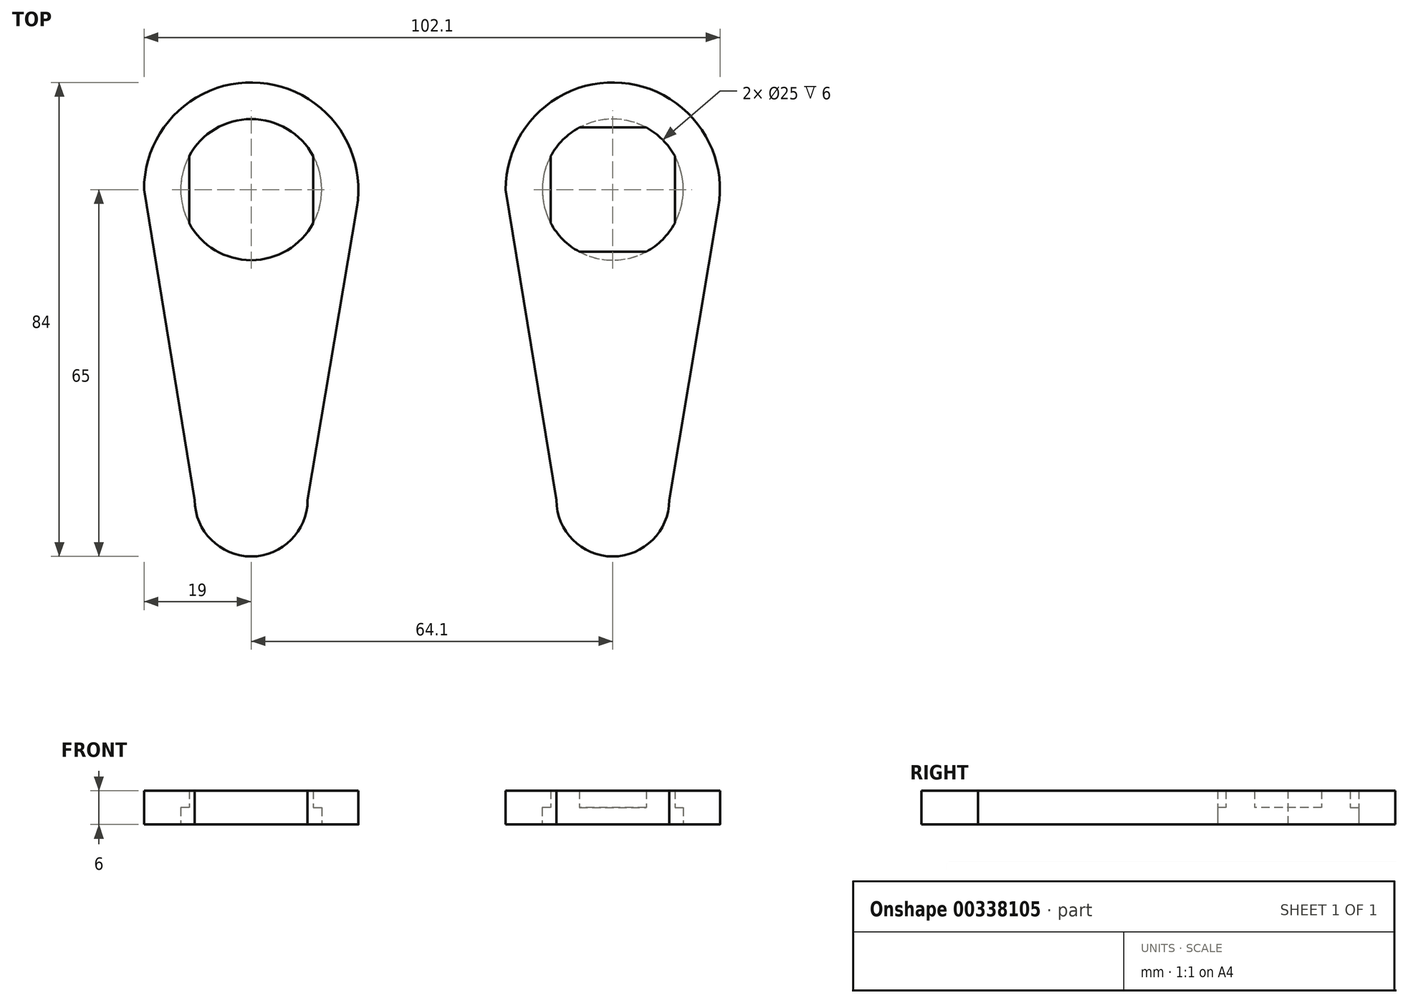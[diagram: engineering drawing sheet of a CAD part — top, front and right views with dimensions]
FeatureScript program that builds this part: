
annotation { "Feature Type Name" : "Feature", "Feature Type Description" : "" }
export const myFeature = defineFeature(function(context is Context, id is Id, definition is map)
    precondition{}
    {
        {
            var Q0;
            Q0=qCreatedBy(makeId("Top.planeOp"),FACE);
            var sketch = newSketch(context, id + "F0", { "sketchPlane" : qUnion([Q0])});
            skLineSegment(sketch, "E0.bottom", {"start": v(-11, 11) * mm, "end": v(11, 11) * mm});
            skLineSegment(sketch, "E0.top", {"start": v(-11, -11) * mm, "end": v(11, -11) * mm});
            skLineSegment(sketch, "E0.left", {"start": v(-11, 11) * mm, "end": v(-11, -11) * mm});
            skLineSegment(sketch, "E0.right", {"start": v(11, 11) * mm, "end": v(11, -11) * mm});
            skCircle(sketch, "E1", {"center": v(0, 0) * mm, "radius": 12.5 * mm});
            skCircle(sketch, "E2", {"center": v(0, 0) * mm, "radius": 19 * mm});
            skCircle(sketch, "E3", {"center": v(0, -55) * mm, "radius": 10 * mm});
            skLineSegment(sketch, "E4", {"start": v(-19, 0) * mm, "end": v(-10, -55) * mm});
            skLineSegment(sketch, "E5", {"start": v(10, -55) * mm, "end": v(19.27, 0) * mm});
            skSolve(sketch);
        }
        {
            var Q0;
            Q0 = qSketchRegion(id + "F0", true);
            var Q1;
            {var subQ0=sQuery(id+"F0.wireOp",EDGE,"E0.left");var subQ1=sQuery(id+"F0.wireOp",EDGE,"E0.bottom");var subQ2=makeQuery(id+"F0.imprint","INTERSECT",VERTEX,{"derivedFrom":[subQ1,subQ0]});Q1=makeQuery(id+"F0.imprint","IMPRINT",FACE,{"disambiguationData":[TD([[makeQuery(id+"F0.imprint","IMPRINT",EDGE,{"disambiguationData":[TD([[subQ2,-1.0]])],"derivedFrom":subQ1}),-1.0]])]});}
            var Q2;
            {var subQ0=sQuery(id+"F0.wireOp",EDGE,"E1");var subQ1=sQuery(id+"F0.wireOp",EDGE,"E0.bottom");var subQ2=makeQuery(id+"F0.imprint","INTERSECT",VERTEX,{"disambiguationData":[OD(0.0)],"derivedFrom":[subQ1,subQ0]});Q2=makeQuery(id+"F0.imprint","IMPRINT",FACE,{"disambiguationData":[TD([[makeQuery(id+"F0.imprint","IMPRINT",EDGE,{"disambiguationData":[TD([[subQ2,-1.0]])],"derivedFrom":subQ1}),1.0]])]});}
            var Q3;
            {var subQ0=sQuery(id+"F0.wireOp",EDGE,"E0.right");var subQ1=sQuery(id+"F0.wireOp",EDGE,"E0.bottom");var subQ2=makeQuery(id+"F0.imprint","INTERSECT",VERTEX,{"derivedFrom":[subQ1,subQ0]});Q3=makeQuery(id+"F0.imprint","IMPRINT",FACE,{"disambiguationData":[TD([[makeQuery(id+"F0.imprint","IMPRINT",EDGE,{"disambiguationData":[TD([[subQ2,1.0]])],"derivedFrom":subQ1}),-1.0]])]});}
            var Q4;
            {var subQ0=sQuery(id+"F0.wireOp",EDGE,"E0.right");var subQ1=sQuery(id+"F0.wireOp",EDGE,"E0.top");var subQ2=makeQuery(id+"F0.imprint","INTERSECT",VERTEX,{"derivedFrom":[subQ1,subQ0]});Q4=makeQuery(id+"F0.imprint","IMPRINT",FACE,{"disambiguationData":[TD([[makeQuery(id+"F0.imprint","IMPRINT",EDGE,{"disambiguationData":[TD([[subQ2,1.0]])],"derivedFrom":subQ1}),1.0]])]});}
            var Q5;
            {var subQ0=sQuery(id+"F0.wireOp",EDGE,"E1");var subQ1=sQuery(id+"F0.wireOp",EDGE,"E0.right");var subQ2=makeQuery(id+"F0.imprint","INTERSECT",VERTEX,{"disambiguationData":[OD(0.0)],"derivedFrom":[subQ1,subQ0]});Q5=makeQuery(id+"F0.imprint","IMPRINT",FACE,{"disambiguationData":[TD([[makeQuery(id+"F0.imprint","IMPRINT",EDGE,{"disambiguationData":[TD([[subQ2,-1.0]])],"derivedFrom":subQ1}),1.0]])]});}
            var Q6;
            {var subQ0=sQuery(id+"F0.wireOp",EDGE,"E0.left");var subQ1=sQuery(id+"F0.wireOp",EDGE,"E0.top");var subQ2=makeQuery(id+"F0.imprint","INTERSECT",VERTEX,{"derivedFrom":[subQ1,subQ0]});Q6=makeQuery(id+"F0.imprint","IMPRINT",FACE,{"disambiguationData":[TD([[makeQuery(id+"F0.imprint","IMPRINT",EDGE,{"disambiguationData":[TD([[subQ2,-1.0]])],"derivedFrom":subQ1}),1.0]])]});}
            var Q7;
            {var subQ0=sQuery(id+"F0.wireOp",EDGE,"E1");var subQ1=sQuery(id+"F0.wireOp",EDGE,"E0.top");var subQ2=makeQuery(id+"F0.imprint","INTERSECT",VERTEX,{"disambiguationData":[OD(0.0)],"derivedFrom":[subQ1,subQ0]});Q7=makeQuery(id+"F0.imprint","IMPRINT",FACE,{"disambiguationData":[TD([[makeQuery(id+"F0.imprint","IMPRINT",EDGE,{"disambiguationData":[TD([[subQ2,-1.0]])],"derivedFrom":subQ1}),-1.0]])]});}
            var Q8;
            {var subQ0=sQuery(id+"F0.wireOp",EDGE,"E1");var subQ1=sQuery(id+"F0.wireOp",EDGE,"E0.left");var subQ2=makeQuery(id+"F0.imprint","INTERSECT",VERTEX,{"disambiguationData":[OD(0.0)],"derivedFrom":[subQ1,subQ0]});Q8=makeQuery(id+"F0.imprint","IMPRINT",FACE,{"disambiguationData":[TD([[makeQuery(id+"F0.imprint","IMPRINT",EDGE,{"disambiguationData":[TD([[subQ2,-1.0]])],"derivedFrom":subQ1}),-1.0]])]});}
            extrude(context, id + "F1", {"entities" : qUnion([Q0, Q1, Q2, Q3, Q4, Q5, Q6, Q7, Q8]), "depth" : 3 * mm});
        }
        {
            var Q0;
            {var subQ1=sQuery(id+"F0.wireOp",EDGE,"E0.left");var subQ5=sQuery(id+"F0.wireOp",EDGE,"E0.bottom");var subQ10=makeQuery(id+"F0.imprint","INTERSECT",VERTEX,{"derivedFrom":[subQ5,subQ1]});Q0=makeQuery(id+"F0.imprint","IMPRINT",FACE,{"disambiguationData":[TD([[makeQuery(id+"F0.imprint","IMPRINT",EDGE,{"disambiguationData":[TD([[subQ10,-1.0]])],"derivedFrom":subQ5}),1.0]])]});}
            var Q1;
            {var subQ0=sQuery(id+"F0.wireOp",EDGE,"E0.left");var subQ1=sQuery(id+"F0.wireOp",EDGE,"E0.bottom");var subQ2=makeQuery(id+"F0.imprint","INTERSECT",VERTEX,{"derivedFrom":[subQ1,subQ0]});Q1=makeQuery(id+"F0.imprint","IMPRINT",FACE,{"disambiguationData":[TD([[makeQuery(id+"F0.imprint","IMPRINT",EDGE,{"disambiguationData":[TD([[subQ2,-1.0]])],"derivedFrom":subQ1}),-1.0]])]});}
            var Q2;
            {var subQ0=sQuery(id+"F0.wireOp",EDGE,"E0.right");var subQ1=sQuery(id+"F0.wireOp",EDGE,"E0.bottom");var subQ2=makeQuery(id+"F0.imprint","INTERSECT",VERTEX,{"derivedFrom":[subQ1,subQ0]});Q2=makeQuery(id+"F0.imprint","IMPRINT",FACE,{"disambiguationData":[TD([[makeQuery(id+"F0.imprint","IMPRINT",EDGE,{"disambiguationData":[TD([[subQ2,1.0]])],"derivedFrom":subQ1}),-1.0]])]});}
            var Q3;
            {var subQ0=sQuery(id+"F0.wireOp",EDGE,"E0.right");var subQ1=sQuery(id+"F0.wireOp",EDGE,"E0.top");var subQ2=makeQuery(id+"F0.imprint","INTERSECT",VERTEX,{"derivedFrom":[subQ1,subQ0]});Q3=makeQuery(id+"F0.imprint","IMPRINT",FACE,{"disambiguationData":[TD([[makeQuery(id+"F0.imprint","IMPRINT",EDGE,{"disambiguationData":[TD([[subQ2,1.0]])],"derivedFrom":subQ1}),1.0]])]});}
            var Q4;
            {var subQ0=sQuery(id+"F0.wireOp",EDGE,"E0.left");var subQ1=sQuery(id+"F0.wireOp",EDGE,"E0.top");var subQ2=makeQuery(id+"F0.imprint","INTERSECT",VERTEX,{"derivedFrom":[subQ1,subQ0]});Q4=makeQuery(id+"F0.imprint","IMPRINT",FACE,{"disambiguationData":[TD([[makeQuery(id+"F0.imprint","IMPRINT",EDGE,{"disambiguationData":[TD([[subQ2,-1.0]])],"derivedFrom":subQ1}),1.0]])]});}
            var Q5;
            {var subQ0=sQuery(id+"F0.wireOp",EDGE,"E5");var subQ1=sQuery(id+"F0.wireOp",EDGE,"E2");var subQ2=makeQuery(id+"F0.imprint","INTERSECT",VERTEX,{"derivedFrom":[subQ1,subQ0]});Q5=makeQuery(id+"F0.imprint","IMPRINT",FACE,{"disambiguationData":[TD([[makeQuery(id+"F0.imprint","IMPRINT",EDGE,{"disambiguationData":[TD([[subQ2,1.0]])],"derivedFrom":subQ1}),-1.0]])]});}
            var Q6;
            {var subQ0=sQuery(id+"F0.wireOp",EDGE,"E3");var subQ1=makeQuery(id+"F0.imprint","INTERSECT",VERTEX,{"derivedFrom":[subQ0,sQuery(id+"F0.wireOp",EDGE,"E4")]});Q6=makeQuery(id+"F0.imprint","IMPRINT",FACE,{"disambiguationData":[TD([[makeQuery(id+"F0.imprint","IMPRINT",EDGE,{"disambiguationData":[TD([[subQ1,1.0]])],"derivedFrom":subQ0}),1.0]])]});}
            extrude(context, id + "F2", {"entities" : qUnion([Q0, Q1, Q2, Q3, Q4, Q5, Q6]), "oppositeDirection" : true, "depth" : 3 * mm});
        }
        {
            var Q0;
            Q0=makeQuery(id+"F1.opExtrude","SWEPT_BODY",BODY,{"disambiguationData":[OSD([sQuery(id+"F0.wireOp",EDGE,"E0.bottom"),sQuery(id+"F0.wireOp",EDGE,"E0.top"),sQuery(id+"F0.wireOp",EDGE,"E0.left"),sQuery(id+"F0.wireOp",EDGE,"E0.right"),sQuery(id+"F0.wireOp",EDGE,"E1"),sQuery(id+"F0.wireOp",EDGE,"E2"),sQuery(id+"F0.wireOp",EDGE,"E3"),sQuery(id+"F0.wireOp",EDGE,"E4"),sQuery(id+"F0.wireOp",EDGE,"E5")])]});
            var Q1;
            Q1=makeQuery(id+"F2.opExtrude","SWEPT_BODY",BODY,{"disambiguationData":[OSD([sQuery(id+"F0.wireOp",EDGE,"E1"),sQuery(id+"F0.wireOp",EDGE,"E2"),sQuery(id+"F0.wireOp",EDGE,"E3"),sQuery(id+"F0.wireOp",EDGE,"E4"),sQuery(id+"F0.wireOp",EDGE,"E5")])]});
            booleanBodies(context, id + "F3", {"operationType" : BooleanOperationType.UNION, "tools" : qUnion([Q0, Q1])});
        }
        {
            var Q0;
            {var subQ0=sQuery(id+"F0.wireOp",EDGE,"E2");var subQ1=sQuery(id+"F0.wireOp",EDGE,"E4");Q0=makeQuery(id+"F3.opBoolean","SPLIT",FACE,{"disambiguationData":[TD([makeQuery(id+"F1.opExtrude","SWEPT_FACE",FACE,{"disambiguationData":[OSD([subQ0])]})])],"derivedFrom":makeQuery(id+"F1.opExtrude","CAP_FACE",FACE,{"disambiguationData":[OSD([sQuery(id+"F0.wireOp",EDGE,"E0.bottom"),sQuery(id+"F0.wireOp",EDGE,"E0.top"),sQuery(id+"F0.wireOp",EDGE,"E0.left"),sQuery(id+"F0.wireOp",EDGE,"E0.right"),sQuery(id+"F0.wireOp",EDGE,"E1"),subQ0,sQuery(id+"F0.wireOp",EDGE,"E3"),subQ1,sQuery(id+"F0.wireOp",EDGE,"E5")])],"isStart":true})});}
            extrude(context, id + "F4", {"entities" : qUnion([Q0]), "operationType" : NewBodyOperationType.REMOVE, "oppositeDirection" : true, "depth" : 25 * mm});
        }
        {
            var Q0;
            Q0=makeQuery(id+"F1.opExtrude","SWEPT_BODY",BODY,{"disambiguationData":[OSD([sQuery(id+"F0.wireOp",EDGE,"E0.bottom"),sQuery(id+"F0.wireOp",EDGE,"E0.top"),sQuery(id+"F0.wireOp",EDGE,"E0.left"),sQuery(id+"F0.wireOp",EDGE,"E0.right"),sQuery(id+"F0.wireOp",EDGE,"E1"),sQuery(id+"F0.wireOp",EDGE,"E2"),sQuery(id+"F0.wireOp",EDGE,"E3"),sQuery(id+"F0.wireOp",EDGE,"E4"),sQuery(id+"F0.wireOp",EDGE,"E5")])]});
            transform(context, id + "F5", {"entities" : qUnion([Q0]), "transformType" : TransformType.TRANSLATION_3D, "dx" : -64.1 * mm, "dy" : 0 * mm, "dz" : 0 * mm, "makeCopy" : true});
        }
        {
            var Q0;
            {var subQ0=sQuery(id+"F0.wireOp",EDGE,"E1");var subQ1=sQuery(id+"F0.wireOp",EDGE,"E0.top");var subQ2=sQuery(id+"F0.wireOp",EDGE,"E0.left");var subQ3=sQuery(id+"F0.wireOp",EDGE,"E0.bottom");var subQ4=sQuery(id+"F0.wireOp",EDGE,"E0.right");Q0=makeQuery(id+"F5.opPattern","COPY",FACE,{"derivedFrom":makeQuery(id+"F3.opBoolean","SPLIT",FACE,{"disambiguationData":[TD([makeQuery(id+"F1.opExtrude","SWEPT_FACE",FACE,{"disambiguationData":[OSD([subQ3])]})])],"derivedFrom":makeQuery(id+"F1.opExtrude","CAP_FACE",FACE,{"disambiguationData":[OSD([subQ3,subQ1,subQ2,subQ4,subQ0,sQuery(id+"F0.wireOp",EDGE,"E2"),sQuery(id+"F0.wireOp",EDGE,"E3"),sQuery(id+"F0.wireOp",EDGE,"E4"),sQuery(id+"F0.wireOp",EDGE,"E5")])],"isStart":true})}),"instanceName":"1"});}
            var Q1;
            {var subQ0=sQuery(id+"F0.wireOp",EDGE,"E1");var subQ1=sQuery(id+"F0.wireOp",EDGE,"E0.bottom");var subQ2=sQuery(id+"F0.wireOp",EDGE,"E0.left");var subQ3=sQuery(id+"F0.wireOp",EDGE,"E0.right");var subQ4=sQuery(id+"F0.wireOp",EDGE,"E0.top");Q1=makeQuery(id+"F5.opPattern","COPY",FACE,{"derivedFrom":makeQuery(id+"F3.opBoolean","SPLIT",FACE,{"disambiguationData":[TD([makeQuery(id+"F1.opExtrude","SWEPT_FACE",FACE,{"disambiguationData":[OSD([subQ4])]})])],"derivedFrom":makeQuery(id+"F1.opExtrude","CAP_FACE",FACE,{"disambiguationData":[OSD([subQ1,subQ4,subQ2,subQ3,subQ0,sQuery(id+"F0.wireOp",EDGE,"E2"),sQuery(id+"F0.wireOp",EDGE,"E3"),sQuery(id+"F0.wireOp",EDGE,"E4"),sQuery(id+"F0.wireOp",EDGE,"E5")])],"isStart":true})}),"instanceName":"1"});}
            extrude(context, id + "F6", {"entities" : qUnion([Q0, Q1]), "operationType" : NewBodyOperationType.REMOVE, "oppositeDirection" : true, "depth" : 25 * mm});
        }
    });
